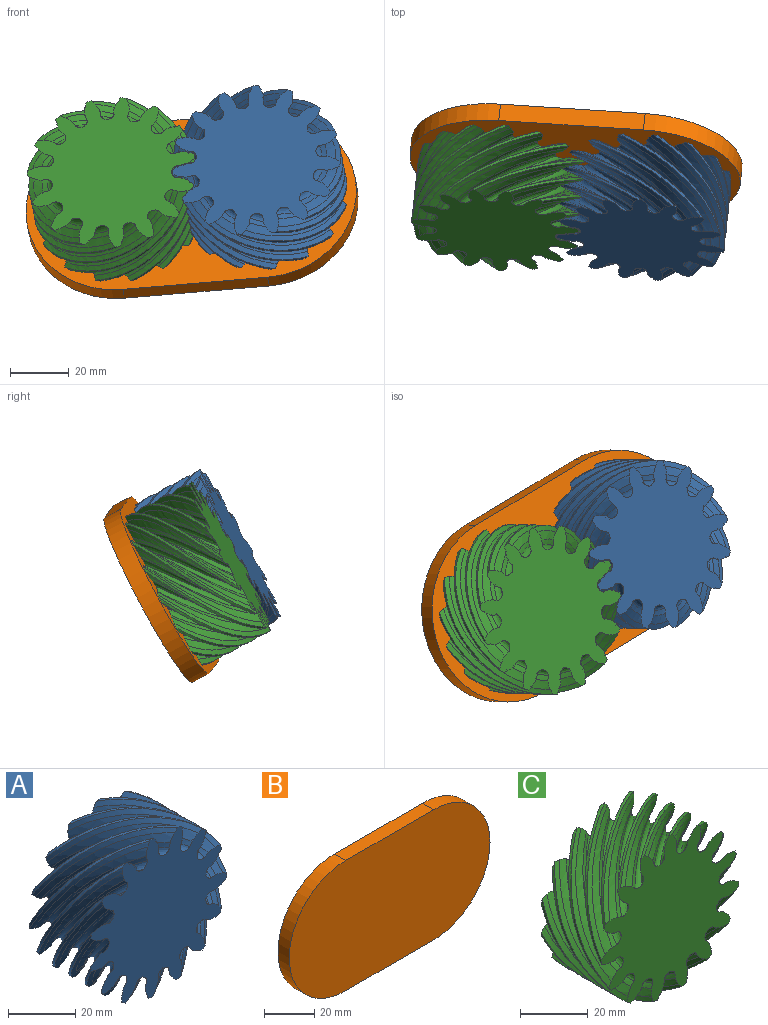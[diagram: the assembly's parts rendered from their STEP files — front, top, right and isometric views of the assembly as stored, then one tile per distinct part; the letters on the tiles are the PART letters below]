
ASSEMBLY  parts=3 mates=2
PART A: 137 faces, bbox 59.3x33x59.2 mm
  f0: bspline ~32.18x28.5mm, area 100.3mm2, adj f2,f3,f8,f11
  f1: bspline ~33.86x31.41mm, area 100.3mm2, adj f2,f3,f7,f12
  f2: plane 58.08x57.82mm, normal (0,1,0), area 1895.9mm2, adj f0,f1,f4,f5,f6,f7,f8,f9
  f3: plane 58.09x57.83mm, normal (0,-1,0), area 1895.9mm2, adj f0,f1,f4,f5,f6,f7,f8,f9
  f4: bspline ~37.52x25.4mm, area 44.8mm2, adj f2,f3,f5,f10
  f5: bspline ~37.3x25.4mm, area 90mm2, adj f2,f3,f4,f6
  f6: bspline ~35.42x25.4mm, area 143.4mm2, adj f2,f3,f5,f7
  f7: bspline ~32.04x25.4mm, area 80.9mm2, adj f1,f2,f3,f6
  f8: bspline ~28.68x25.4mm, area 80.9mm2, adj f0,f2,f3,f9
  f9: bspline ~33.05x25.4mm, area 143.4mm2, adj f2,f3,f8,f10
  f10: bspline ~35.85x25.4mm, area 90mm2, adj f2,f3,f4,f9
  f11: bspline ~31.41x27.23mm, area 100.3mm2, adj f0,f2,f3,f133
  f12: bspline ~35.1x32.18mm, area 100.3mm2, adj f1,f2,f3,f18
  f13: bspline ~35.38x31.41mm, area 100.3mm2, adj f2,f3,f17,f21
  f14: bspline ~41.9x25.4mm, area 44.8mm2, adj f2,f3,f15,f20
  f15: bspline ~40.71x25.4mm, area 90mm2, adj f2,f3,f14,f16
  f16: bspline ~38.3x25.4mm, area 143.4mm2, adj f2,f3,f15,f17
  f17: bspline ~34.06x25.4mm, area 80.9mm2, adj f2,f3,f13,f16
  f18: bspline ~33.73x25.4mm, area 80.9mm2, adj f2,f3,f12,f19
  f19: bspline ~38.07x25.4mm, area 143.4mm2, adj f2,f3,f18,f20
  f20: bspline ~40.6x25.4mm, area 90mm2, adj f2,f3,f14,f19
  f21: bspline ~35.63x32.18mm, area 100.3mm2, adj f2,f3,f13,f27
  f22: bspline ~31.41x30.78mm, area 100.3mm2, adj f2,f3,f26,f30
  f23: bspline ~39.03x25.4mm, area 44.8mm2, adj f2,f3,f24,f29
  f24: bspline ~37.41x25.4mm, area 90mm2, adj f2,f3,f23,f25
  f25: bspline ~34.63x25.4mm, area 143.4mm2, adj f2,f3,f24,f26
  f26: bspline ~30.2x25.4mm, area 80.9mm2, adj f2,f3,f22,f25
  f27: bspline ~32.95x25.4mm, area 80.9mm2, adj f2,f3,f21,f28
  f28: bspline ~36.52x25.4mm, area 143.4mm2, adj f2,f3,f27,f29
  f29: bspline ~38.49x25.4mm, area 90mm2, adj f2,f3,f23,f28
  f30: bspline ~32.18x30.36mm, area 100.3mm2, adj f2,f3,f22,f36
  f31: bspline ~31.41x29.28mm, area 100.3mm2, adj f2,f3,f35,f39
  f32: bspline ~30.02x29.64mm, area 44.8mm2, adj f2,f3,f33,f38
  f33: bspline ~30.8x27.87mm, area 90mm2, adj f2,f3,f32,f34
  f34: bspline ~29.87x25.4mm, area 143.4mm2, adj f2,f3,f33,f35
  f35: bspline ~26.82x25.4mm, area 80.9mm2, adj f2,f3,f31,f34
  f36: bspline ~26.48x25.4mm, area 80.9mm2, adj f2,f3,f30,f37
  f37: bspline ~29.51x25.76mm, area 143.4mm2, adj f2,f3,f36,f38
  f38: bspline ~30.38x28.26mm, area 90mm2, adj f2,f3,f32,f37
  f39: bspline ~32.18x30.67mm, area 100.3mm2, adj f2,f3,f31,f45
  f40: bspline ~34.81x31.41mm, area 100.3mm2, adj f2,f3,f44,f48
  f41: bspline ~39.27x25.4mm, area 44.8mm2, adj f2,f3,f42,f47
  f42: bspline ~38.67x25.4mm, area 90mm2, adj f2,f3,f41,f43
  f43: bspline ~36.7x25.4mm, area 143.4mm2, adj f2,f3,f42,f44
  f44: bspline ~33.09x25.4mm, area 80.9mm2, adj f2,f3,f40,f43
  f45: bspline ~30.45x25.4mm, area 80.9mm2, adj f2,f3,f39,f46
  f46: bspline ~34.89x25.4mm, area 143.4mm2, adj f2,f3,f45,f47
  f47: bspline ~37.67x25.4mm, area 90mm2, adj f2,f3,f41,f46
  f48: bspline ~35.82x32.18mm, area 100.3mm2, adj f2,f3,f40,f54
  f49: bspline ~34.79x31.41mm, area 100.3mm2, adj f2,f3,f53,f57
  f50: bspline ~41.86x25.4mm, area 44.8mm2, adj f2,f3,f51,f56
  f51: bspline ~40.54x25.4mm, area 90mm2, adj f2,f3,f50,f52
  f52: bspline ~38x25.4mm, area 143.4mm2, adj f2,f3,f51,f53
  f53: bspline ~33.64x25.4mm, area 80.9mm2, adj f2,f3,f49,f52
  f54: bspline ~34.1x25.4mm, area 80.9mm2, adj f2,f3,f48,f55
  f55: bspline ~38.31x25.4mm, area 143.4mm2, adj f2,f3,f54,f56
  f56: bspline ~40.69x25.4mm, area 90mm2, adj f2,f3,f50,f55
  f57: bspline ~34.78x32.18mm, area 100.3mm2, adj f2,f3,f49,f63
  f58: bspline ~31.41x28.75mm, area 100.3mm2, adj f2,f3,f62,f66
  f59: bspline ~37.21x25.4mm, area 44.8mm2, adj f2,f3,f60,f65
  f60: bspline ~35.53x25.4mm, area 90mm2, adj f2,f3,f59,f61
  f61: bspline ~32.73x25.4mm, area 143.4mm2, adj f2,f3,f60,f62
  f62: bspline ~28.37x25.4mm, area 80.9mm2, adj f2,f3,f58,f61
  f63: bspline ~31.84x25.4mm, area 80.9mm2, adj f2,f3,f57,f64
  f64: bspline ~35.21x25.4mm, area 143.4mm2, adj f2,f3,f63,f65
  f65: bspline ~37.05x25.4mm, area 90mm2, adj f2,f3,f59,f64
  f66: bspline ~32.18x28.37mm, area 100.3mm2, adj f2,f3,f58,f72
  f67: bspline ~31.41x31.06mm, area 100.3mm2, adj f2,f3,f71,f75
  f68: bspline ~32.8x26.95mm, area 44.8mm2, adj f2,f3,f69,f74
  f69: bspline ~33.34x25.4mm, area 90mm2, adj f2,f3,f68,f70
  f70: bspline ~32.01x25.4mm, area 143.4mm2, adj f2,f3,f69,f71
  f71: bspline ~28.88x25.4mm, area 80.9mm2, adj f2,f3,f67,f70
  f72: bspline ~25.4x24.2mm, area 80.9mm2, adj f2,f3,f66,f73
  f73: bspline ~28.3x27.25mm, area 143.4mm2, adj f2,f3,f72,f74
  f74: bspline ~31.05x27.93mm, area 90mm2, adj f2,f3,f68,f73
  f75: bspline ~32.51x32.18mm, area 100.3mm2, adj f2,f3,f67,f81
  f76: bspline ~35.39x31.41mm, area 100.3mm2, adj f2,f3,f80,f84
  f77: bspline ~40.6x25.4mm, area 44.8mm2, adj f2,f3,f78,f83
  f78: bspline ~39.73x25.4mm, area 90mm2, adj f2,f3,f77,f79
  f79: bspline ~37.65x25.4mm, area 143.4mm2, adj f2,f3,f78,f80
  f80: bspline ~33.79x25.4mm, area 80.9mm2, adj f2,f3,f76,f79
  f81: bspline ~31.9x25.4mm, area 80.9mm2, adj f2,f3,f75,f82
  f82: bspline ~36.35x25.4mm, area 143.4mm2, adj f2,f3,f81,f83
  f83: bspline ~39.08x25.4mm, area 90mm2, adj f2,f3,f77,f82
  f84: bspline ~36.16x32.18mm, area 100.3mm2, adj f2,f3,f76,f90
  f85: bspline ~33.82x31.41mm, area 100.3mm2, adj f2,f3,f89,f93
  f86: bspline ~41.37x25.4mm, area 44.8mm2, adj f2,f3,f87,f92
  f87: bspline ~39.93x25.4mm, area 90mm2, adj f2,f3,f86,f88
  f88: bspline ~37.28x25.4mm, area 143.4mm2, adj f2,f3,f87,f89
  f89: bspline ~32.85x25.4mm, area 80.9mm2, adj f2,f3,f85,f88
  f90: bspline ~34.09x25.4mm, area 80.9mm2, adj f2,f3,f84,f91
  f91: bspline ~38.13x25.4mm, area 143.4mm2, adj f2,f3,f90,f92
  f92: bspline ~40.34x25.4mm, area 90mm2, adj f2,f3,f86,f91
  f93: bspline ~33.55x32.18mm, area 100.3mm2, adj f2,f3,f85,f99
  f94: bspline ~31.41x26.48mm, area 100.3mm2, adj f2,f3,f98,f102
  f95: bspline ~34.99x25.4mm, area 44.8mm2, adj f2,f3,f96,f101
  f96: bspline ~33.26x25.72mm, area 90mm2, adj f2,f3,f95,f97
  f97: bspline ~30.47x25.4mm, area 143.4mm2, adj f2,f3,f96,f98
  f98: bspline ~26.23x25.4mm, area 80.9mm2, adj f2,f3,f94,f97
  f99: bspline ~30.38x25.4mm, area 80.9mm2, adj f2,f3,f93,f100
  f100: bspline ~33.6x25.4mm, area 143.4mm2, adj f2,f3,f99,f101
  f101: bspline ~35.2x25.4mm, area 90mm2, adj f2,f3,f95,f100
  f102: bspline ~32.18x26.31mm, area 100.3mm2, adj f2,f3,f94,f108
  f103: bspline ~32.53x31.41mm, area 100.3mm2, adj f2,f3,f107,f111
  f104: bspline ~35.36x25.4mm, area 44.8mm2, adj f2,f3,f105,f110
  f105: bspline ~35.51x25.4mm, area 90mm2, adj f2,f3,f104,f106
  f106: bspline ~33.87x25.4mm, area 143.4mm2, adj f2,f3,f105,f107
  f107: bspline ~30.63x25.4mm, area 80.9mm2, adj f2,f3,f103,f106
  f108: bspline ~26.58x25.4mm, area 80.9mm2, adj f2,f3,f102,f109
  f109: bspline ~30.84x25.4mm, area 143.4mm2, adj f2,f3,f108,f110
  f110: bspline ~33.64x25.4mm, area 90mm2, adj f2,f3,f104,f109
  f111: bspline ~33.99x32.18mm, area 100.3mm2, adj f2,f3,f103,f117
  f112: bspline ~35.58x31.41mm, area 100.3mm2, adj f2,f3,f116,f120
  f113: bspline ~41.47x25.4mm, area 44.8mm2, adj f2,f3,f114,f119
  f114: bspline ~40.43x25.4mm, area 90mm2, adj f2,f3,f113,f115
  f115: bspline ~38.18x25.4mm, area 143.4mm2, adj f2,f3,f114,f116
  f116: bspline ~34.11x25.4mm, area 80.9mm2, adj f2,f3,f112,f115
  f117: bspline ~33x25.4mm, area 80.9mm2, adj f2,f3,f111,f118
  f118: bspline ~37.42x25.4mm, area 143.4mm2, adj f2,f3,f117,f119
  f119: bspline ~40.06x25.4mm, area 90mm2, adj f2,f3,f113,f118
  f120: bspline ~36.09x32.18mm, area 100.3mm2, adj f2,f3,f112,f126
  f121: bspline ~32.48x31.41mm, area 100.3mm2, adj f2,f3,f125,f129
  f122: bspline ~40.42x25.4mm, area 44.8mm2, adj f2,f3,f123,f128
  f123: bspline ~38.89x25.4mm, area 90mm2, adj f2,f3,f122,f124
  f124: bspline ~36.15x25.4mm, area 143.4mm2, adj f2,f3,f123,f125
  f125: bspline ~31.7x25.4mm, area 80.9mm2, adj f2,f3,f121,f124
  f126: bspline ~33.7x25.4mm, area 80.9mm2, adj f2,f3,f120,f127
  f127: bspline ~37.53x25.4mm, area 143.4mm2, adj f2,f3,f126,f128
  f128: bspline ~39.59x25.4mm, area 90mm2, adj f2,f3,f122,f127
  f129: bspline ~32.18x32.07mm, area 100.3mm2, adj f2,f3,f121,f134
  f130: bspline ~32.38x27.38mm, area 44.8mm2, adj f2,f3,f131,f136
  f131: bspline ~30.62x28.31mm, area 90mm2, adj f2,f3,f130,f132
  f132: bspline ~27.87x27.57mm, area 143.4mm2, adj f2,f3,f131,f133
  f133: bspline ~25.4x24.47mm, area 80.9mm2, adj f2,f3,f11,f132
  f134: bspline ~28.59x25.4mm, area 80.9mm2, adj f2,f3,f129,f135
  f135: bspline ~31.7x25.4mm, area 143.4mm2, adj f2,f3,f134,f136
  f136: bspline ~32.97x25.63mm, area 90mm2, adj f2,f3,f130,f135
PART B: 6 faces, bbox 113x6.4x63.5 mm
  f0: cylinder r=31.75mm len=63.5mm, axis (0,1,0), area 633.4mm2, adj f1,f3,f4,f5
  f1: plane 49.53x6.35mm, normal (0,0,-1), area 314.5mm2, adj f0,f2,f4,f5
  f2: cylinder r=31.75mm len=63.5mm, axis (0,1,0), area 633.4mm2, adj f1,f3,f4,f5
  f3: plane 49.53x6.35mm, normal (0,0,1), area 314.5mm2, adj f0,f2,f4,f5
  f4: plane 113.03x63.5mm, normal (0,-1,0), area 6312.1mm2, adj f0,f1,f2,f3
  f5: plane 113.03x63.5mm, normal (0,1,0), area 6312.1mm2, adj f0,f1,f2,f3
PART C: 137 faces, bbox 59.3x33x59.2 mm
  f0: bspline ~32.25x32.18mm, area 100.3mm2, adj f2,f3,f5,f11
  f1: bspline ~35.33x31.41mm, area 100.3mm2, adj f2,f3,f4,f12
  f2: plane 58.09x57.83mm, normal (0,-1,0), area 1895.9mm2, adj f0,f1,f4,f5,f6,f7,f8,f9
  f3: plane 58.08x57.82mm, normal (0,1,0), area 1895.9mm2, adj f0,f1,f4,f5,f6,f7,f8,f9
  f4: bspline ~33.7x25.4mm, area 80.9mm2, adj f1,f2,f3,f10
  f5: bspline ~31.7x25.4mm, area 80.9mm2, adj f0,f2,f3,f6
  f6: bspline ~36.15x25.4mm, area 143.4mm2, adj f2,f3,f5,f7
  f7: bspline ~38.89x25.4mm, area 90mm2, adj f2,f3,f6,f8
  f8: bspline ~40.42x25.4mm, area 44.8mm2, adj f2,f3,f7,f9
  f9: bspline ~39.59x25.4mm, area 90mm2, adj f2,f3,f8,f10
  f10: bspline ~37.53x25.4mm, area 143.4mm2, adj f2,f3,f4,f9
  f11: bspline ~31.41x30.81mm, area 100.3mm2, adj f0,f2,f3,f130
  f12: bspline ~36.13x32.18mm, area 100.3mm2, adj f1,f2,f3,f15
  f13: bspline ~33.99x31.41mm, area 100.3mm2, adj f2,f3,f14,f21
  f14: bspline ~33x25.4mm, area 80.9mm2, adj f2,f3,f13,f20
  f15: bspline ~34.11x25.4mm, area 80.9mm2, adj f2,f3,f12,f16
  f16: bspline ~38.18x25.4mm, area 143.4mm2, adj f2,f3,f15,f17
  f17: bspline ~40.43x25.4mm, area 90mm2, adj f2,f3,f16,f18
  f18: bspline ~41.47x25.4mm, area 44.8mm2, adj f2,f3,f17,f19
  f19: bspline ~40.06x25.4mm, area 90mm2, adj f2,f3,f18,f20
  f20: bspline ~37.42x25.4mm, area 143.4mm2, adj f2,f3,f14,f19
  f21: bspline ~33.77x32.18mm, area 100.3mm2, adj f2,f3,f13,f24
  f22: bspline ~31.41x26.83mm, area 100.3mm2, adj f2,f3,f23,f30
  f23: bspline ~26.58x25.4mm, area 80.9mm2, adj f2,f3,f22,f29
  f24: bspline ~30.63x25.4mm, area 80.9mm2, adj f2,f3,f21,f25
  f25: bspline ~33.87x25.4mm, area 143.4mm2, adj f2,f3,f24,f26
  f26: bspline ~35.51x25.4mm, area 90mm2, adj f2,f3,f25,f27
  f27: bspline ~35.36x25.4mm, area 44.8mm2, adj f2,f3,f26,f28
  f28: bspline ~33.64x25.4mm, area 90mm2, adj f2,f3,f27,f29
  f29: bspline ~30.84x25.4mm, area 143.4mm2, adj f2,f3,f23,f28
  f30: bspline ~32.18x26.63mm, area 100.3mm2, adj f2,f3,f22,f33
  f31: bspline ~32.31x31.41mm, area 100.3mm2, adj f2,f3,f32,f39
  f32: bspline ~30.38x25.4mm, area 80.9mm2, adj f2,f3,f31,f38
  f33: bspline ~26.23x25.4mm, area 80.9mm2, adj f2,f3,f30,f34
  f34: bspline ~30.47x25.4mm, area 143.4mm2, adj f2,f3,f33,f35
  f35: bspline ~33.26x25.72mm, area 90mm2, adj f2,f3,f34,f36
  f36: bspline ~34.99x25.4mm, area 44.8mm2, adj f2,f3,f35,f37
  f37: bspline ~35.2x25.4mm, area 90mm2, adj f2,f3,f36,f38
  f38: bspline ~33.6x25.4mm, area 143.4mm2, adj f2,f3,f32,f37
  f39: bspline ~33.78x32.18mm, area 100.3mm2, adj f2,f3,f31,f42
  f40: bspline ~35.58x31.41mm, area 100.3mm2, adj f2,f3,f41,f48
  f41: bspline ~34.09x25.4mm, area 80.9mm2, adj f2,f3,f40,f47
  f42: bspline ~32.85x25.4mm, area 80.9mm2, adj f2,f3,f39,f43
  f43: bspline ~37.28x25.4mm, area 143.4mm2, adj f2,f3,f42,f44
  f44: bspline ~39.93x25.4mm, area 90mm2, adj f2,f3,f43,f45
  f45: bspline ~41.37x25.4mm, area 44.8mm2, adj f2,f3,f44,f46
  f46: bspline ~40.34x25.4mm, area 90mm2, adj f2,f3,f45,f47
  f47: bspline ~38.13x25.4mm, area 143.4mm2, adj f2,f3,f41,f46
  f48: bspline ~36.13x32.18mm, area 100.3mm2, adj f2,f3,f40,f51
  f49: bspline ~32.71x31.41mm, area 100.3mm2, adj f2,f3,f50,f57
  f50: bspline ~31.9x25.4mm, area 80.9mm2, adj f2,f3,f49,f56
  f51: bspline ~33.79x25.4mm, area 80.9mm2, adj f2,f3,f48,f52
  f52: bspline ~37.65x25.4mm, area 143.4mm2, adj f2,f3,f51,f53
  f53: bspline ~39.73x25.4mm, area 90mm2, adj f2,f3,f52,f54
  f54: bspline ~40.6x25.4mm, area 44.8mm2, adj f2,f3,f53,f55
  f55: bspline ~39.08x25.4mm, area 90mm2, adj f2,f3,f54,f56
  f56: bspline ~36.35x25.4mm, area 143.4mm2, adj f2,f3,f50,f55
  f57: bspline ~32.3x32.18mm, area 100.3mm2, adj f2,f3,f49,f60
  f58: bspline ~31.41x26.9mm, area 100.3mm2, adj f2,f3,f59,f66
  f59: bspline ~25.4x24.2mm, area 80.9mm2, adj f2,f3,f58,f65
  f60: bspline ~28.88x25.4mm, area 80.9mm2, adj f2,f3,f57,f61
  f61: bspline ~32.01x25.4mm, area 143.4mm2, adj f2,f3,f60,f62
  f62: bspline ~33.34x25.4mm, area 90mm2, adj f2,f3,f61,f63
  f63: bspline ~32.8x26.95mm, area 44.8mm2, adj f2,f3,f62,f64
  f64: bspline ~31.05x27.93mm, area 90mm2, adj f2,f3,f63,f65
  f65: bspline ~28.3x27.25mm, area 143.4mm2, adj f2,f3,f59,f64
  f66: bspline ~32.18x28.14mm, area 100.3mm2, adj f2,f3,f58,f69
  f67: bspline ~33.68x31.41mm, area 100.3mm2, adj f2,f3,f68,f75
  f68: bspline ~31.84x25.4mm, area 80.9mm2, adj f2,f3,f67,f74
  f69: bspline ~28.37x25.4mm, area 80.9mm2, adj f2,f3,f66,f70
  f70: bspline ~32.73x25.4mm, area 143.4mm2, adj f2,f3,f69,f71
  f71: bspline ~35.53x25.4mm, area 90mm2, adj f2,f3,f70,f72
  f72: bspline ~37.21x25.4mm, area 44.8mm2, adj f2,f3,f71,f73
  f73: bspline ~37.05x25.4mm, area 90mm2, adj f2,f3,f72,f74
  f74: bspline ~35.21x25.4mm, area 143.4mm2, adj f2,f3,f68,f73
  f75: bspline ~34.95x32.18mm, area 100.3mm2, adj f2,f3,f67,f78
  f76: bspline ~35.43x31.41mm, area 100.3mm2, adj f2,f3,f77,f84
  f77: bspline ~34.1x25.4mm, area 80.9mm2, adj f2,f3,f76,f83
  f78: bspline ~33.64x25.4mm, area 80.9mm2, adj f2,f3,f75,f79
  f79: bspline ~38x25.4mm, area 143.4mm2, adj f2,f3,f78,f80
  f80: bspline ~40.54x25.4mm, area 90mm2, adj f2,f3,f79,f81
  f81: bspline ~41.86x25.4mm, area 44.8mm2, adj f2,f3,f80,f82
  f82: bspline ~40.69x25.4mm, area 90mm2, adj f2,f3,f81,f83
  f83: bspline ~38.31x25.4mm, area 143.4mm2, adj f2,f3,f77,f82
  f84: bspline ~35.73x32.18mm, area 100.3mm2, adj f2,f3,f76,f87
  f85: bspline ~31.41x31.07mm, area 100.3mm2, adj f2,f3,f86,f93
  f86: bspline ~30.45x25.4mm, area 80.9mm2, adj f2,f3,f85,f92
  f87: bspline ~33.09x25.4mm, area 80.9mm2, adj f2,f3,f84,f88
  f88: bspline ~36.7x25.4mm, area 143.4mm2, adj f2,f3,f87,f89
  f89: bspline ~38.67x25.4mm, area 90mm2, adj f2,f3,f88,f90
  f90: bspline ~39.27x25.4mm, area 44.8mm2, adj f2,f3,f89,f91
  f91: bspline ~37.67x25.4mm, area 90mm2, adj f2,f3,f90,f92
  f92: bspline ~34.89x25.4mm, area 143.4mm2, adj f2,f3,f86,f91
  f93: bspline ~32.18x30.64mm, area 100.3mm2, adj f2,f3,f85,f96
  f94: bspline ~31.41x28.98mm, area 100.3mm2, adj f2,f3,f95,f102
  f95: bspline ~26.48x25.4mm, area 80.9mm2, adj f2,f3,f94,f101
  f96: bspline ~26.82x25.4mm, area 80.9mm2, adj f2,f3,f93,f97
  f97: bspline ~29.87x25.4mm, area 143.4mm2, adj f2,f3,f96,f98
  f98: bspline ~30.8x27.87mm, area 90mm2, adj f2,f3,f97,f99
  f99: bspline ~30.02x29.64mm, area 44.8mm2, adj f2,f3,f98,f100
  f100: bspline ~30.38x28.26mm, area 90mm2, adj f2,f3,f99,f101
  f101: bspline ~29.51x25.76mm, area 143.4mm2, adj f2,f3,f95,f100
  f102: bspline ~32.18x30.36mm, area 100.3mm2, adj f2,f3,f94,f105
  f103: bspline ~34.69x31.41mm, area 100.3mm2, adj f2,f3,f104,f111
  f104: bspline ~32.95x25.4mm, area 80.9mm2, adj f2,f3,f103,f110
  f105: bspline ~30.2x25.4mm, area 80.9mm2, adj f2,f3,f102,f106
  f106: bspline ~34.63x25.4mm, area 143.4mm2, adj f2,f3,f105,f107
  f107: bspline ~37.41x25.4mm, area 90mm2, adj f2,f3,f106,f108
  f108: bspline ~39.03x25.4mm, area 44.8mm2, adj f2,f3,f107,f109
  f109: bspline ~38.49x25.4mm, area 90mm2, adj f2,f3,f108,f110
  f110: bspline ~36.52x25.4mm, area 143.4mm2, adj f2,f3,f104,f109
  f111: bspline ~35.74x32.18mm, area 100.3mm2, adj f2,f3,f103,f114
  f112: bspline ~34.9x31.41mm, area 100.3mm2, adj f2,f3,f113,f120
  f113: bspline ~33.73x25.4mm, area 80.9mm2, adj f2,f3,f112,f119
  f114: bspline ~34.06x25.4mm, area 80.9mm2, adj f2,f3,f111,f115
  f115: bspline ~38.3x25.4mm, area 143.4mm2, adj f2,f3,f114,f116
  f116: bspline ~40.71x25.4mm, area 90mm2, adj f2,f3,f115,f117
  f117: bspline ~41.9x25.4mm, area 44.8mm2, adj f2,f3,f116,f118
  f118: bspline ~40.6x25.4mm, area 90mm2, adj f2,f3,f117,f119
  f119: bspline ~38.07x25.4mm, area 143.4mm2, adj f2,f3,f113,f118
  f120: bspline ~34.94x32.18mm, area 100.3mm2, adj f2,f3,f112,f123
  f121: bspline ~31.41x29.08mm, area 100.3mm2, adj f2,f3,f122,f129
  f122: bspline ~28.68x25.4mm, area 80.9mm2, adj f2,f3,f121,f128
  f123: bspline ~32.04x25.4mm, area 80.9mm2, adj f2,f3,f120,f124
  f124: bspline ~35.42x25.4mm, area 143.4mm2, adj f2,f3,f123,f125
  f125: bspline ~37.3x25.4mm, area 90mm2, adj f2,f3,f124,f126
  f126: bspline ~37.52x25.4mm, area 44.8mm2, adj f2,f3,f125,f127
  f127: bspline ~35.85x25.4mm, area 90mm2, adj f2,f3,f126,f128
  f128: bspline ~33.05x25.4mm, area 143.4mm2, adj f2,f3,f122,f127
  f129: bspline ~32.18x28.68mm, area 100.3mm2, adj f2,f3,f121,f131
  f130: bspline ~28.59x25.4mm, area 80.9mm2, adj f2,f3,f11,f136
  f131: bspline ~25.4x24.47mm, area 80.9mm2, adj f2,f3,f129,f132
  f132: bspline ~27.87x27.57mm, area 143.4mm2, adj f2,f3,f131,f133
  f133: bspline ~30.62x28.31mm, area 90mm2, adj f2,f3,f132,f134
  f134: bspline ~32.38x27.38mm, area 44.8mm2, adj f2,f3,f133,f135
  f135: bspline ~32.97x25.63mm, area 90mm2, adj f2,f3,f134,f136
  f136: bspline ~31.7x25.4mm, area 143.4mm2, adj f2,f3,f130,f135
PLACE A rot(axis=(-0.82,-0.57,-0.02),34.8deg) t=(5.89,-47.68,5.39)mm
PLACE B rot(axis=(-0.98,-0.13,-0.17),28.8deg) t=(-15.67,-18.19,-11.55)mm
PLACE C rot(axis=(-0.14,0.95,-0.28),105.1deg) t=(-40.91,-22.16,-10.66)mm
MATE revolute C.f3 <-> B.f0  axis (0.1,0.88,-0.47) through (-40.91,-22.16,-10.66)mm
MATE revolute A.f2 <-> B.f2  axis (0.1,0.88,-0.47) through (8.34,-25.37,-6.5)mm
